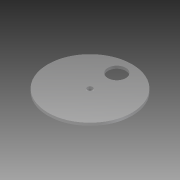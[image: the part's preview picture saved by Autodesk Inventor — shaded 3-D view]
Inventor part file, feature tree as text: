
AUTODESK INVENTOR PART (.ipt)
format: ipt  version: 2015 (Build 190159000, 159)  size: 79,872 bytes
history: native  units: mm
features: extrude x1, sketch x1
ambient origin geometry x8: Origin, YZ Plane, XZ Plane, XY Plane, X Axis, Y Axis, Z Axis, Center Point
bodies: Body1 (feature_tree)
feature tree (2):
  extrude  "Extrusion2"  Depth=3.0mm
  sketch  "Sketch1"  dims[d0=98.0mm d1=5.9mm d4=20.0mm d5=30.0mm d6=3.0mm d7=0.0mm]
